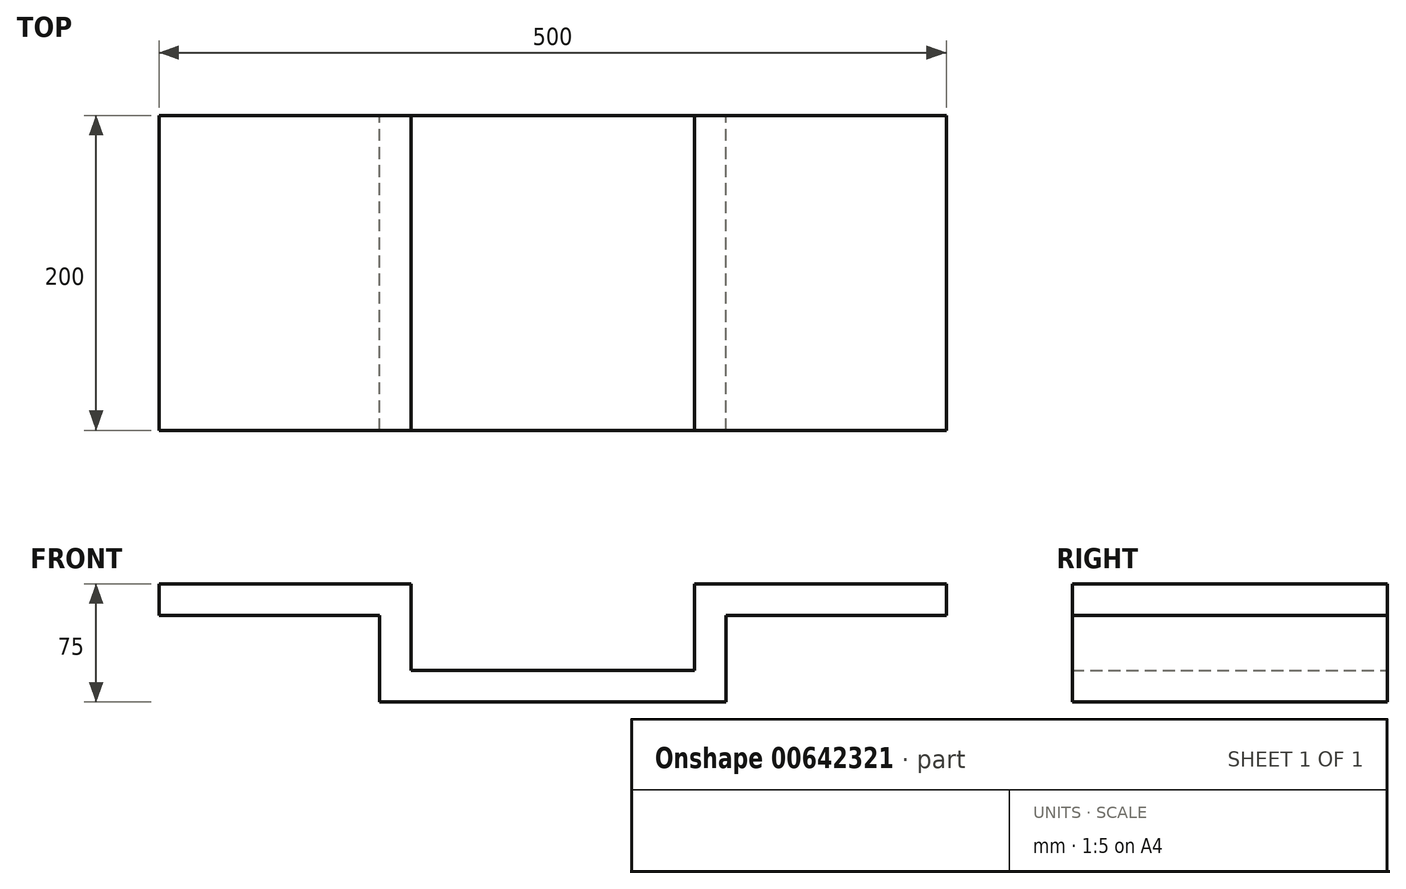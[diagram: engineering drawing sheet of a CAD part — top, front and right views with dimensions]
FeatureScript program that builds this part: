
annotation { "Feature Type Name" : "Feature", "Feature Type Description" : "" }
export const myFeature = defineFeature(function(context is Context, id is Id, definition is map)
    precondition{}
    {
        {
            var Q0;
            Q0=qCreatedBy(makeId("Front.planeOp"),FACE);
            var sketch = newSketch(context, id + "F0", { "sketchPlane" : qUnion([Q0])});
            skLineSegment(sketch, "E0", {"start": v(-250, 75) * mm, "end": v(-90, 75) * mm});
            skLineSegment(sketch, "E1", {"start": v(-90, 75) * mm, "end": v(-90, 20) * mm});
            skLineSegment(sketch, "E2", {"start": v(-90, 20) * mm, "end": v(90, 20) * mm});
            skLineSegment(sketch, "E3", {"start": v(90, 20) * mm, "end": v(90, 75) * mm});
            skLineSegment(sketch, "E4", {"start": v(90, 75) * mm, "end": v(250, 75) * mm});
            skLineSegment(sketch, "E5", {"start": v(250, 75) * mm, "end": v(250, 55) * mm});
            skLineSegment(sketch, "E6", {"start": v(250, 55) * mm, "end": v(110, 55) * mm});
            skLineSegment(sketch, "E7", {"start": v(110, 55) * mm, "end": v(110, 0) * mm});
            skLineSegment(sketch, "E8", {"start": v(110, 0) * mm, "end": v(0, 0) * mm});
            skLineSegment(sketch, "E9", {"start": v(0, 0) * mm, "end": v(-110, 0) * mm});
            skLineSegment(sketch, "E10", {"start": v(-110, 0) * mm, "end": v(-110, 55) * mm});
            skLineSegment(sketch, "E11", {"start": v(-110, 55) * mm, "end": v(-250, 55) * mm});
            skLineSegment(sketch, "E12", {"start": v(-250, 55) * mm, "end": v(-250, 75) * mm});
            skSolve(sketch);
        }
        {
            var Q0;
            Q0=makeQuery(id+"F0.imprint","IMPRINT",FACE,{"disambiguationData":[TD([[makeQuery(id+"F0.imprint","IMPRINT",EDGE,{"derivedFrom":sQuery(id+"F0.wireOp",EDGE,"E0")}),-1.0]])]});
            extrude(context, id + "F1", {"entities" : qUnion([Q0]), "depth" : 200 * mm, "offsetDistance" : 25 * mm});
        }
    });
